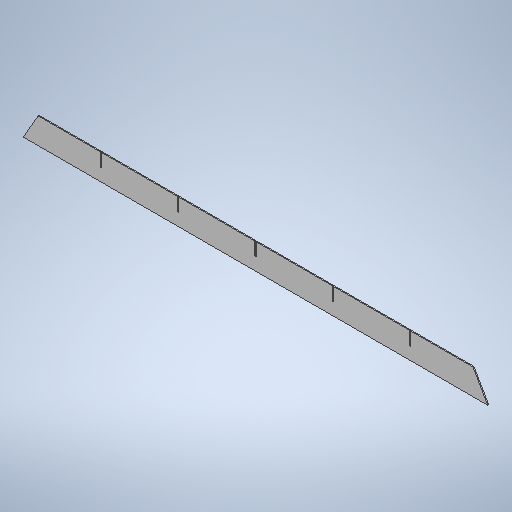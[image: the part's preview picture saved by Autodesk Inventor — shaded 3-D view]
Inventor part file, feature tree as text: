
AUTODESK INVENTOR PART (.ipt)
format: ipt  version: 2025 (Build 290162010, 162A)  size: 322,048 bytes
history: native  units: mm
features: other x3, sketch x2, sheet_metal_op x1, extrude x1, pattern_linear x1
ambient origin geometry x8: Origin, YZ Plane, XZ Plane, XY Plane, X Axis, Y Axis, Z Axis, Center Point
bodies: Solid1 (feature_tree)
feature tree (8):
  other  "MSC 203 GRID"
  sheet_metal_op  "Face1"
  extrude  "Extrusion1"  Depth=80.0mm
  pattern_linear  "Rectangular Pattern1"  Spacing1=120.0deg  [1 undecoded]
  sketch  "Sketch1"  dims[d0=80.0mm d1=1800.0mm]
  other  "Plate1"
  sketch  "Sketch2"  dims[d2=3.0mm d3=120.0deg d6=674.96mm d7=120.0deg d8=674.96mm d9=3.2mm d10=41.0mm d11=0.0mm d12=0.0mm d13=50.0mm d15=240.0mm]
  other  "Definition1"
note: 1 required parameter value undecoded (feature->parameter linkage not recoverable at this tier; creation-order binding heuristic only, values carry confidence <= 0.55)
